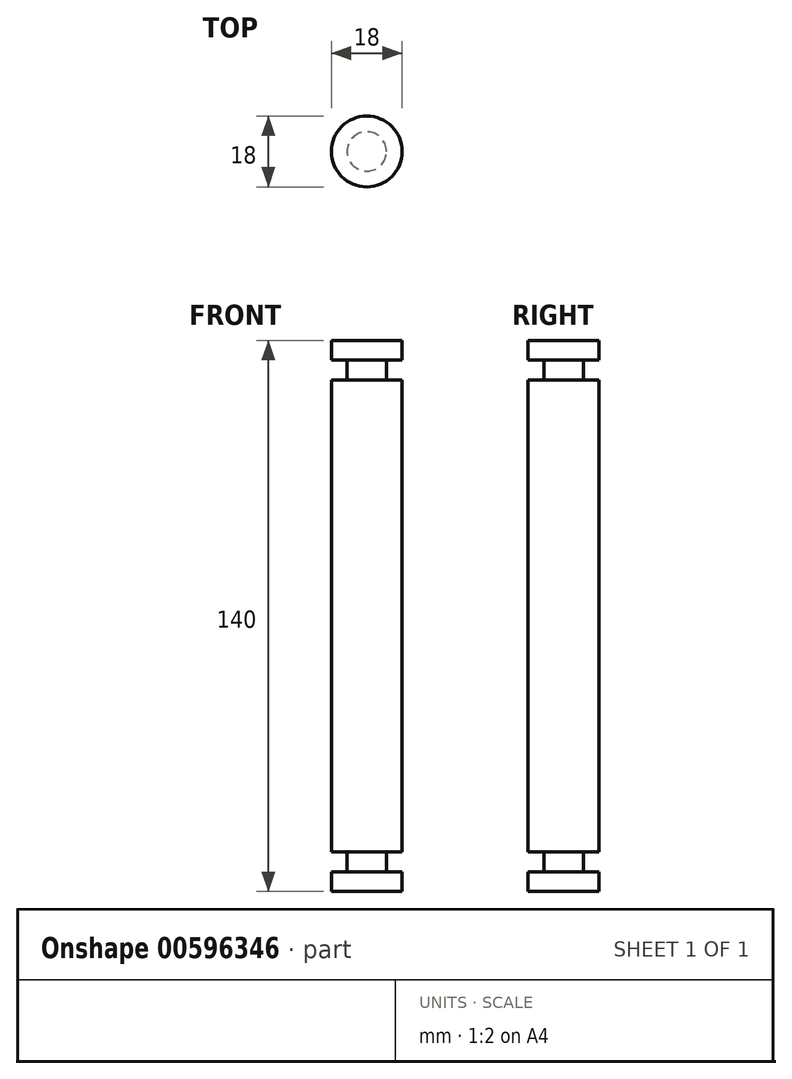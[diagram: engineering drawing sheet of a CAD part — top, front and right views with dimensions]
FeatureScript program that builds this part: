
annotation { "Feature Type Name" : "Feature", "Feature Type Description" : "" }
export const myFeature = defineFeature(function(context is Context, id is Id, definition is map)
    precondition{}
    {
        {
            var Q0;
            Q0=qCreatedBy(makeId("Top.planeOp"),FACE);
            var sketch = newSketch(context, id + "F0", { "sketchPlane" : qUnion([Q0])});
            skCircle(sketch, "E0", {"center": v(0, 0) * mm, "radius": 9 * mm});
            skSolve(sketch);
        }
        {
            var Q0;
            Q0=makeQuery(id+"F0.imprint","IMPRINT",FACE,{"disambiguationData":[TD([[makeQuery(id+"F0.imprint","IMPRINT",EDGE,{"derivedFrom":sQuery(id+"F0.wireOp",EDGE,"E0")}),1.0]])]});
            extrude(context, id + "F1", {"entities" : qUnion([Q0]), "depth" : 120 * mm, "offsetDistance" : 25 * mm});
        }
        {
            var Q0;
            Q0=makeQuery(id+"F1.opExtrude","CAP_FACE",FACE,{"disambiguationData":[OSD([sQuery(id+"F0.wireOp",EDGE,"E0")])],"isStart":false});
            var sketch = newSketch(context, id + "F2", { "sketchPlane" : qUnion([Q0])});
            skCircle(sketch, "E1", {"center": v(0, 0) * mm, "radius": 5 * mm});
            skSolve(sketch);
        }
        {
            var Q0;
            Q0=makeQuery(id+"F2.imprint","IMPRINT",FACE,{"disambiguationData":[TD([[makeQuery(id+"F2.imprint","IMPRINT",EDGE,{"derivedFrom":sQuery(id+"F2.wireOp",EDGE,"E1")}),1.0]])]});
            extrude(context, id + "F3", {"entities" : qUnion([Q0]), "operationType" : NewBodyOperationType.ADD, "depth" : 5 * mm, "offsetDistance" : 25 * mm});
        }
        {
            var Q0;
            Q0=makeQuery(id+"F3.opExtrude","CAP_FACE",FACE,{"disambiguationData":[OSD([sQuery(id+"F2.wireOp",EDGE,"E1")])],"isStart":false});
            var sketch = newSketch(context, id + "F4", { "sketchPlane" : qUnion([Q0])});
            skCircle(sketch, "E2", {"center": v(0, 0) * mm, "radius": 9 * mm});
            skSolve(sketch);
        }
        {
            var Q0;
            Q0=makeQuery(id+"F4.imprint","IMPRINT",FACE,{"disambiguationData":[TD([[makeQuery(id+"F4.imprint","IMPRINT",EDGE,{"derivedFrom":sQuery(id+"F4.wireOp",EDGE,"E2")}),1.0]])]});
            var Q1;
            Q1=makeQuery(id+"F4.imprint","IMPRINT",FACE,{"disambiguationData":[TD([[makeQuery(id+"F4.imprint","IMPRINT",EDGE,{"derivedFrom":makeQuery(id+"F3.opExtrude","CAP_EDGE",EDGE,{"disambiguationData":[OSD([sQuery(id+"F2.wireOp",EDGE,"E1")])],"isStart":false})}),1.0]])]});
            extrude(context, id + "F5", {"entities" : qUnion([Q0, Q1]), "depth" : 5 * mm, "offsetDistance" : 25 * mm});
        }
        {
            var Q0;
            Q0=makeQuery(id+"F1.opExtrude","CAP_FACE",FACE,{"disambiguationData":[OSD([sQuery(id+"F0.wireOp",EDGE,"E0")])],"isStart":true});
            var sketch = newSketch(context, id + "F6", { "sketchPlane" : qUnion([Q0])});
            skCircle(sketch, "E3", {"center": v(0, 0) * mm, "radius": 5 * mm});
            skSolve(sketch);
        }
        {
            var Q0;
            Q0=makeQuery(id+"F6.imprint","IMPRINT",FACE,{"disambiguationData":[TD([[makeQuery(id+"F6.imprint","IMPRINT",EDGE,{"derivedFrom":sQuery(id+"F6.wireOp",EDGE,"E3")}),1.0]])]});
            extrude(context, id + "F7", {"entities" : qUnion([Q0]), "operationType" : NewBodyOperationType.ADD, "depth" : 5 * mm, "offsetDistance" : 25 * mm});
        }
        {
            var Q0;
            Q0=makeQuery(id+"F7.opExtrude","CAP_FACE",FACE,{"disambiguationData":[OSD([sQuery(id+"F6.wireOp",EDGE,"E3")])],"isStart":false});
            var sketch = newSketch(context, id + "F8", { "sketchPlane" : qUnion([Q0])});
            skCircle(sketch, "E4", {"center": v(0, 0) * mm, "radius": 9 * mm});
            skSolve(sketch);
        }
        {
            var Q0;
            Q0=makeQuery(id+"F8.imprint","IMPRINT",FACE,{"disambiguationData":[TD([[makeQuery(id+"F8.imprint","IMPRINT",EDGE,{"derivedFrom":sQuery(id+"F8.wireOp",EDGE,"E4")}),1.0]])]});
            var Q1;
            Q1=makeQuery(id+"F8.imprint","IMPRINT",FACE,{"disambiguationData":[TD([[makeQuery(id+"F8.imprint","IMPRINT",EDGE,{"derivedFrom":makeQuery(id+"F7.opExtrude","CAP_EDGE",EDGE,{"disambiguationData":[OSD([sQuery(id+"F6.wireOp",EDGE,"E3")])],"isStart":false})}),1.0]])]});
            extrude(context, id + "F9", {"entities" : qUnion([Q0, Q1]), "operationType" : NewBodyOperationType.ADD, "depth" : 5 * mm, "offsetDistance" : 25 * mm});
        }
    });
